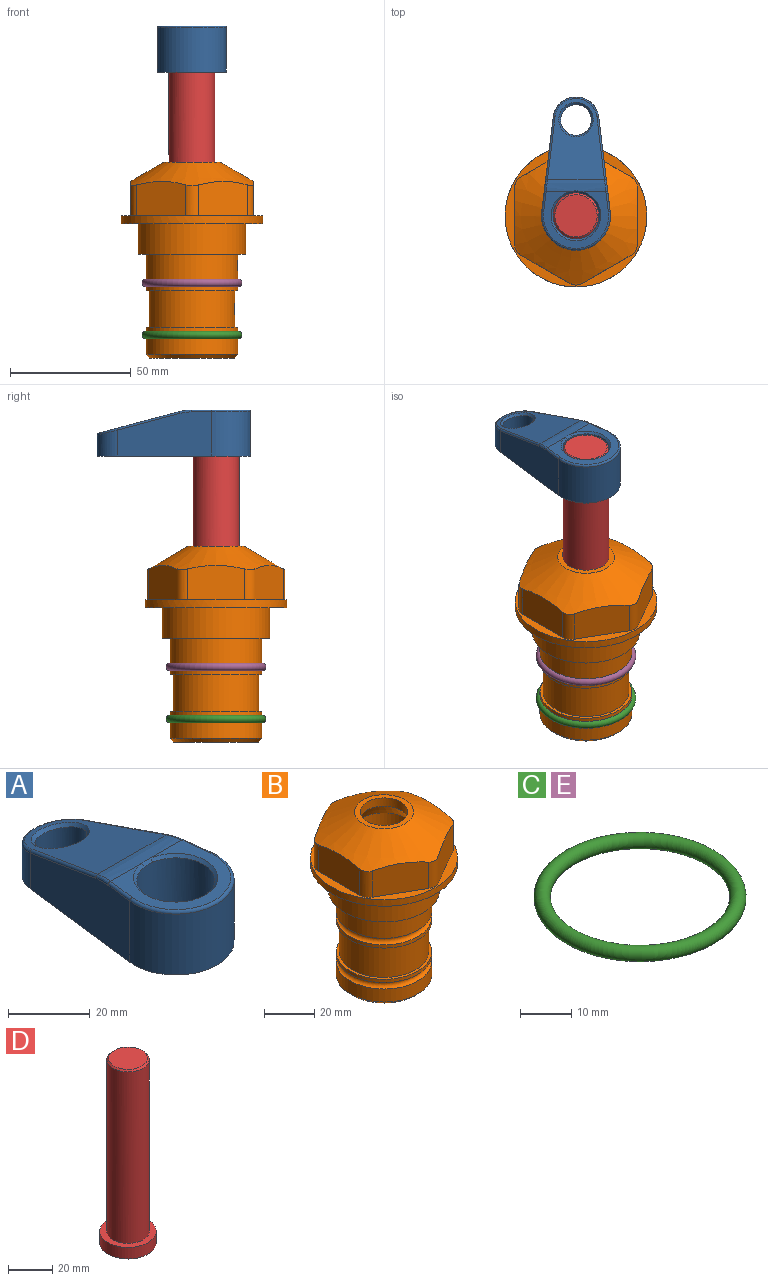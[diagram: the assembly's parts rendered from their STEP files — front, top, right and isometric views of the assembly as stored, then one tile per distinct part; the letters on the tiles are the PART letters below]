
ASSEMBLY  parts=5 mates=4
PART A: 31 faces, bbox 31.7x65.5x19.8 mm
  f0: plane 39.12x18.26mm, normal (0.99,0.12,0), area 612.2mm2, adj f1,f4,f7,f11,f13,f15
  f1: cylinder r=9.53mm len=18.91mm, axis (0,0,-1), area 296.1mm2, adj f0,f2,f7,f17
  f2: plane 39.12x18.26mm, normal (-0.99,0.12,0), area 612.2mm2, adj f1,f4,f7,f12,f14,f16
  f3: cylinder r=6.35mm len=12.7mm, axis (0,0,-1), area 362.4mm2, adj f7,f18
  f4: cylinder r=14.29mm len=28.58mm, axis (0,0,-1), area 882.2mm2, adj f0,f2,f7,f10
  f5: cylinder r=9.53mm len=19.05mm, axis (0,0,-1), area 1092.6mm2, adj f7,f19,f20
  f6: plane 26.99x23.69mm, normal (0,0,1), area 216.2mm2, adj f9,f10,f11,f12,f19
  f7: plane 63.5x28.58mm, normal (0,0,-1), area 661.8mm2, adj f0,f1,f2,f3,f4,f5,f22,f23
  f8: plane 33.52x23.6mm, normal (0,0.26,0.97), area 486mm2, adj f9,f15,f16,f17,f18
  f9: cylinder r=19.05mm len=24.72mm, axis (1,0,0), area 120.4mm2, adj f6,f8,f13,f14,f20
  f10: torus R=13.49mm, axis (0,0,1), area 59mm2, adj f4,f6,f11,f12
  f11: cylinder r=0.79mm len=8.67mm, axis (0.12,-0.99,0), area 10.8mm2, adj f0,f6,f10,f13
  f12: cylinder r=0.79mm len=8.67mm, axis (0.12,0.99,0), area 10.8mm2, adj f2,f6,f10,f14
  f13: bspline ~4.95x1.42mm, area 6.1mm2, adj f0,f9,f11,f15
  f14: bspline ~4.95x1.42mm, area 6.1mm2, adj f2,f9,f12,f16
  f15: cylinder r=0.79mm len=25.95mm, axis (0.12,-0.96,0.26), area 32.9mm2, adj f0,f8,f13,f17
  f16: cylinder r=0.79mm len=25.95mm, axis (0.12,0.96,-0.26), area 32.9mm2, adj f2,f8,f14,f17
  f17: bspline ~18.91x8.38mm, area 30mm2, adj f1,f8,f15,f16
  f18: bspline ~14.29x14.29mm, area 48.3mm2, adj f3,f8
  f19: cone r=9.53mm half-angle=45deg, axis (0,0,1), area 66.5mm2, adj f5,f6,f20
  f20: bspline ~3.22x0.96mm, area 3.5mm2, adj f5,f9,f19
  f21: plane 2.75x2.72mm, normal (0,0,-1), area 2.9mm2, adj f23,f25,f28
  f22: plane 23.05x15.88mm, normal (-0.99,-0.12,0), area 323.6mm2, adj f7,f25,f26,f27,f28,f29
  f23: plane 23.05x15.88mm, normal (0.99,-0.12,0), area 323.6mm2, adj f7,f21,f25,f27,f28,f30
  f24: cylinder r=9.53mm len=10.69mm, axis (0,0,-1), area 114.7mm2, adj f7,f27,f29,f30
  f25: cylinder r=12.7mm len=20.59mm, axis (0,0,-1), area 381.1mm2, adj f7,f21,f22,f23,f26,f28
  f26: plane 2.75x2.72mm, normal (0,0,-1), area 2.9mm2, adj f22,f25,f28
  f27: plane 19.72x18.37mm, normal (0,-0.26,-0.97), area 291.8mm2, adj f22,f23,f24,f28,f29,f30
  f28: cylinder r=15.88mm len=19.92mm, axis (1,0,0), area 54.8mm2, adj f21,f22,f23,f25,f26,f27
  f29: cylinder r=1.59mm len=11mm, axis (0,0,-1), area 34.7mm2, adj f7,f22,f24,f27
  f30: cylinder r=1.59mm len=11mm, axis (0,0,-1), area 34.7mm2, adj f7,f23,f24,f27
PART B: 36 faces, bbox 58.7x58.7x81 mm
  f0: cylinder r=17.78mm len=35.56mm, axis (0,0,1), area 1670.8mm2, adj f23,f24,f31
  f1: cylinder r=19.05mm len=38.1mm, axis (0,0,1), area 1191.9mm2, adj f26,f27,f30
  f2: plane 58.66x58.66mm, normal (0,0,-1), area 1150.6mm2, adj f3,f28
  f3: cylinder r=29.33mm len=58.66mm, axis (0,0,-1), area 585.1mm2, adj f2,f4
  f4: plane 58.66x58.66mm, normal (0,0,1), area 475.9mm2, adj f3,f5,f6,f7,f8,f9,f10,f11
  f5: plane 20.32x14.34mm, normal (-0.5,0.87,0), area 324.4mm2, adj f4,f15,f16,f17
  f6: plane 20.32x14.34mm, normal (0.5,0.87,0), area 324.4mm2, adj f4,f14,f15,f17
  f7: plane 23.48x14.34mm, normal (1,0,0), area 324.4mm2, adj f4,f13,f14,f17
  f8: plane 20.32x14.34mm, normal (0.5,-0.87,0), area 324.4mm2, adj f4,f12,f13,f17
  f9: plane 20.32x14.34mm, normal (-0.5,-0.87,0), area 324.4mm2, adj f4,f11,f12,f17
  f10: plane 23.48x14.34mm, normal (-1,0,0), area 324.4mm2, adj f4,f11,f16,f17
  f11: cylinder r=5.08mm len=12.85mm, axis (0,0,-1), area 67.2mm2, adj f4,f9,f10,f17
  f12: cylinder r=5.08mm len=12.85mm, axis (0,0,-1), area 67.2mm2, adj f4,f8,f9,f17
  f13: cylinder r=5.08mm len=12.85mm, axis (0,0,-1), area 67.2mm2, adj f4,f7,f8,f17
  f14: cylinder r=5.08mm len=12.85mm, axis (0,0,-1), area 67.2mm2, adj f4,f6,f7,f17
  f15: cylinder r=5.08mm len=12.85mm, axis (0,0,-1), area 67.2mm2, adj f4,f5,f6,f17
  f16: cylinder r=5.08mm len=12.85mm, axis (0,0,-1), area 67.2mm2, adj f4,f5,f10,f17
  f17: cone r=11.73mm half-angle=60deg, axis (0,0,-1), area 2071.8mm2, adj f5,f6,f7,f8,f9,f10,f11,f12
  f18: plane 23.46x23.46mm, normal (0,0,1), area 147.4mm2, adj f17,f35
  f19: plane 34.93x34.93mm, normal (0,0,-1), area 958mm2, adj f29
  f20: cylinder r=19.05mm len=38.1mm, axis (0,0,1), area 760.1mm2, adj f21,f29
  f21: torus R=19.05mm, axis (0,0,1), area 565.3mm2, adj f20,f22
  f22: cylinder r=19.05mm len=38.1mm, axis (0,0,1), area 190mm2, adj f21,f23
  f23: plane 38.1x38.1mm, normal (0,0,1), area 146.9mm2, adj f0,f22
  f24: plane 38.1x38.1mm, normal (0,0,-1), area 146.9mm2, adj f0,f25
  f25: cylinder r=19.05mm len=38.1mm, axis (0,0,1), area 190mm2, adj f24,f26
  f26: torus R=19.05mm, axis (0,0,1), area 565.3mm2, adj f1,f25
  f27: plane 44.45x44.45mm, normal (0,0,-1), area 411.7mm2, adj f1,f28
  f28: cylinder r=22.23mm len=44.45mm, axis (0,0,1), area 1773.5mm2, adj f2,f27
  f29: cone r=19.05mm half-angle=45deg, axis (0,0,1), area 257.5mm2, adj f19,f20
  f30: cylinder r=3.17mm len=6.75mm, axis (-1,0,0), area 128mm2, adj f1,f33
  f31: cylinder r=3.17mm len=6.35mm, axis (-1,0,0), area 102.5mm2, adj f0,f33
  f32: plane 25.4x25.4mm, normal (0,0,1), area 506.7mm2, adj f33
  f33: cylinder r=12.7mm len=66.42mm, axis (0,0,-1), area 5236.2mm2, adj f30,f31,f32,f34
  f34: cone r=9.53mm half-angle=30deg, axis (0,0,-1), area 443.4mm2, adj f33,f35
  f35: cylinder r=9.53mm len=19.05mm, axis (0,0,-1), area 240.9mm2, adj f18,f34
PART C: 1 faces, bbox 44.7x44.7x3.2 mm
  f0: torus R=19.05mm, axis (0,0,1), area 1193.9mm2
PART D: 6 faces, bbox 25.4x25.4x101.6 mm
  f0: plane 17.46x17.46mm, normal (0,0,1), area 239.5mm2, adj f5
  f1: plane 25.4x25.4mm, normal (0,0,-1), area 506.7mm2, adj f2
  f2: cylinder r=12.7mm len=25.4mm, axis (0,0,1), area 506.7mm2, adj f1,f3
  f3: plane 25.4x25.4mm, normal (0,0,1), area 221.7mm2, adj f2,f4
  f4: cylinder r=9.53mm len=94.46mm, axis (0,0,1), area 5653mm2, adj f3,f5
  f5: cone r=8.73mm half-angle=45deg, axis (0,0,-1), area 64.4mm2, adj f0,f4
PART E: same geometry as C
PLACE A t=(0,0,73.98)mm
PLACE B t=(0,0,55.63)mm
PLACE C t=(0,0,34.04)mm
PLACE D t=(0,0,73.18)mm
PLACE E t=(0,0,55.63)mm
MATE fastened B.f0 <-> C.f0  axis (0,0,1) through (0,0,9.53)mm
MATE fastened B.f0 <-> E.f0  axis (0,0,1) through (0,0,31.12)mm
MATE cylindrical D.f2 <-> B.f0  axis (0,0,-1) through (0,0,35.08)mm
MATE fastened D.f2 <-> A.f4  axis (0,0,1) through (0,0,136.68)mm
